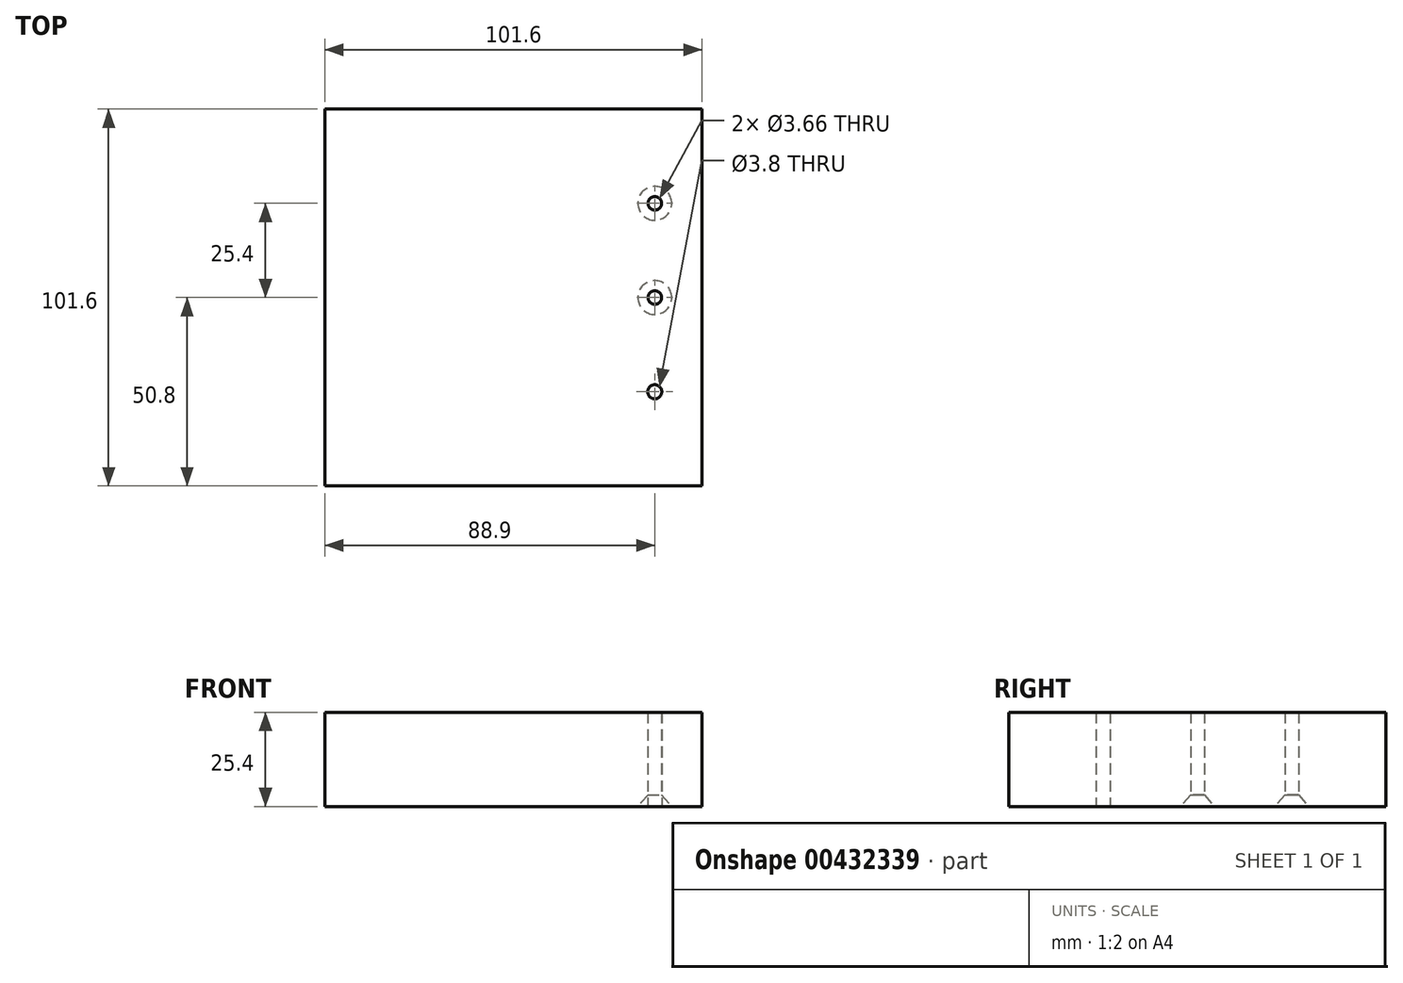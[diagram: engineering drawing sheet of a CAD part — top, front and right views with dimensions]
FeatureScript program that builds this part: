
annotation { "Feature Type Name" : "Feature", "Feature Type Description" : "" }
export const myFeature = defineFeature(function(context is Context, id is Id, definition is map)
    precondition{}
    {
        {
            var Q0;
            Q0=qCreatedBy(makeId("Top.planeOp"),FACE);
            var sketch = newSketch(context, id + "F0", { "sketchPlane" : qUnion([Q0])});
            skLineSegment(sketch, "E0.bottom", {"start": v(50.8, -50.8) * mm, "end": v(-50.8, -50.8) * mm});
            skLineSegment(sketch, "E0.top", {"start": v(50.8, 50.8) * mm, "end": v(-50.8, 50.8) * mm});
            skLineSegment(sketch, "E0.left", {"start": v(50.8, -50.8) * mm, "end": v(50.8, 50.8) * mm});
            skLineSegment(sketch, "E0.right", {"start": v(-50.8, -50.8) * mm, "end": v(-50.8, 50.8) * mm});
            skPoint(sketch, "E0.middle", {"position": v(0, 0) * mm});
            skPoint(sketch, "E1", {"position": v(-38.1, 25.4) * mm});
            skPoint(sketch, "E2", {"position": v(0, 25.4) * mm});
            skPoint(sketch, "E3", {"position": v(38.1, 25.4) * mm});
            skPoint(sketch, "E4", {"position": v(-38.1, -25.4) * mm});
            skPoint(sketch, "E5", {"position": v(0, -25.4) * mm});
            skPoint(sketch, "E6", {"position": v(38.1, 0) * mm});
            skPoint(sketch, "E7", {"position": v(38.1, -25.4) * mm});
            skSolve(sketch);
        }
        {
            var Q0;
            Q0 = qSketchRegion(id + "F0", true);
            extrude(context, id + "F1", {"entities" : qUnion([Q0]), "depth" : 25.4 * mm});
        }
        {
            var Q0;
            Q0=sQuery(id+"F0.wireOp",VERTEX,"E7");
            var Q1;
            Q1=makeQuery(id+"F1.opExtrude","SWEPT_BODY",BODY,{"disambiguationData":[OSD([sQuery(id+"F0.wireOp",EDGE,"E0.bottom"),sQuery(id+"F0.wireOp",EDGE,"E0.top"),sQuery(id+"F0.wireOp",EDGE,"E0.left"),sQuery(id+"F0.wireOp",EDGE,"E0.right")])]});
            hole(context, id + "F2", {"style" : HoleStyle.SIMPLE, "endStyle" : HoleEndStyle.THROUGH, "oppositeDirection" : true, "standardTappedOrClearance" : lookupTablePath({ "standard" : "ANSI", "fit" : "Normal (ASME)", "size" : "#6", "type" : "Clearance" }), "standardBlindInLast" : lookupTablePath({ "fit" : "Free", "standard" : "ANSI", "size" : "#6", "type" : "Clearance" }), "holeDiameter" : 3.8 * mm, "isTappedThrough" : true, "tappedDepth" : 12.7 * mm, "tapClearance" : 3, "locations" : qUnion([Q0]), "scope" : qUnion([Q1])});
        }
        {
            var Q0;
            Q0=sQuery(id+"F0.wireOp",VERTEX,"E6");
            var Q1;
            Q1=sQuery(id+"F0.wireOp",VERTEX,"E3");
            var Q2;
            Q2=makeQuery(id+"F1.opExtrude","SWEPT_BODY",BODY,{"disambiguationData":[OSD([sQuery(id+"F0.wireOp",EDGE,"E0.bottom"),sQuery(id+"F0.wireOp",EDGE,"E0.top"),sQuery(id+"F0.wireOp",EDGE,"E0.left"),sQuery(id+"F0.wireOp",EDGE,"E0.right")])]});
            hole(context, id + "F3", {"style" : HoleStyle.C_SINK, "endStyle" : HoleEndStyle.THROUGH, "oppositeDirection" : true, "standardTappedOrClearance" : lookupTablePath({ "standard" : "ANSI", "engagement" : "50%", "pitch" : "32 tpi", "size" : "#8", "type" : "Tapped" }), "standardBlindInLast" : lookupTablePath({ "standard" : "ANSI", "engagement" : "50%", "pitch" : "32 tpi", "size" : "#8", "type" : "Tapped" }), "holeDiameter" : 3.66 * mm, "cSinkDiameter" : 9.12 * mm, "cSinkAngle" : 82 * degree, "showTappedDepth" : true, "isTappedThrough" : true, "tappedDepth" : 12.7 * mm, "tapClearance" : 3, "locations" : qUnion([Q0, Q1]), "scope" : qUnion([Q2]), "majorDiameter" : 4.17 * mm});
        }
    });
